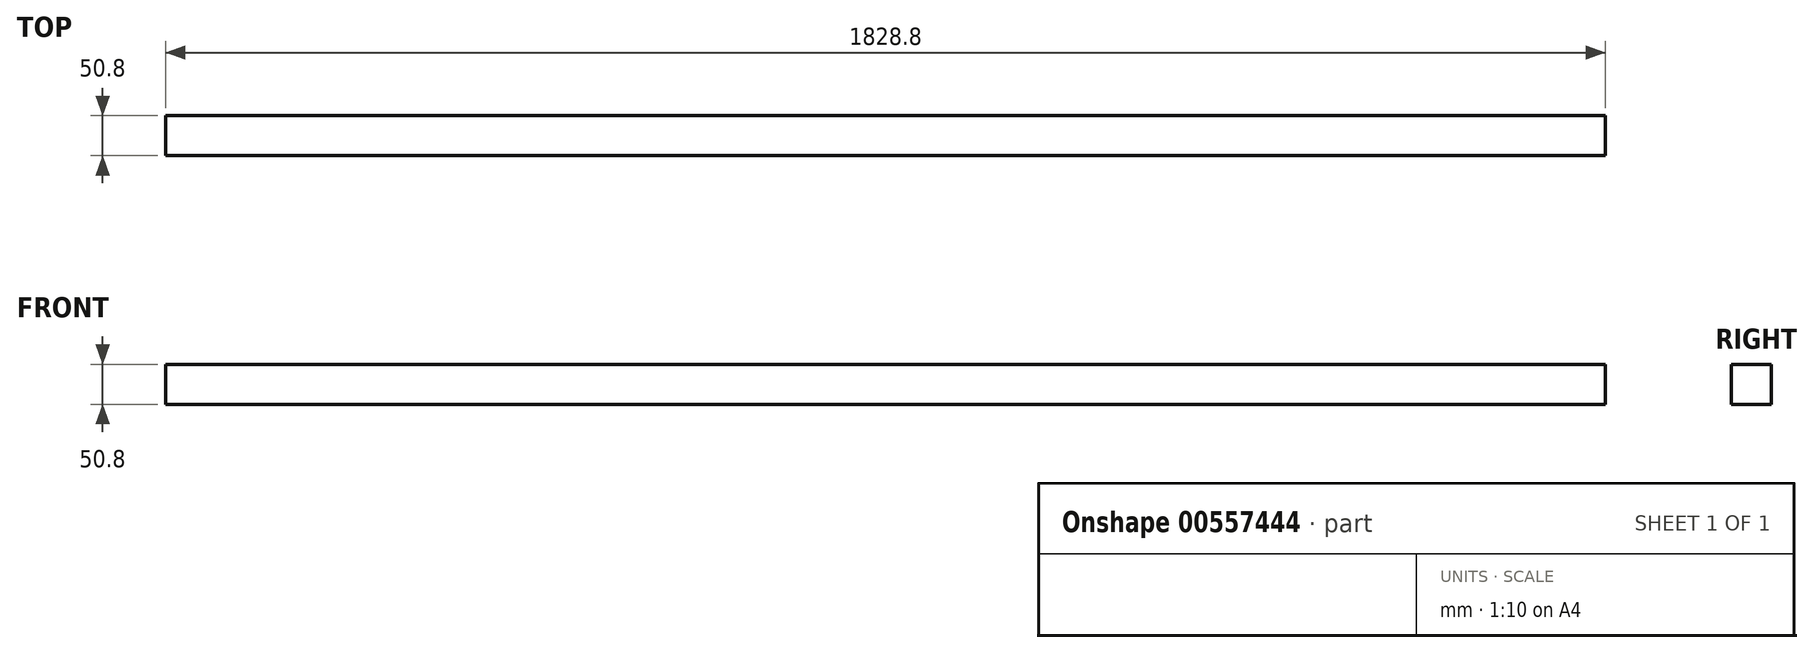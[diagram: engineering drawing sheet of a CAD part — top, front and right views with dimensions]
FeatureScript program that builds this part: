
annotation { "Feature Type Name" : "Feature", "Feature Type Description" : "" }
export const myFeature = defineFeature(function(context is Context, id is Id, definition is map)
    precondition{}
    {
        {
            var Q0;
            Q0=qCreatedBy(makeId("Front.planeOp"),FACE);
            var sketch = newSketch(context, id + "F0", { "sketchPlane" : qUnion([Q0])});
            skLineSegment(sketch, "E0.bottom", {"start": v(0, 50.8) * mm, "end": v(1828.8, 50.8) * mm});
            skLineSegment(sketch, "E0.top", {"start": v(0, 0) * mm, "end": v(1828.8, 0) * mm});
            skLineSegment(sketch, "E0.left", {"start": v(0, 50.8) * mm, "end": v(0, 0) * mm});
            skLineSegment(sketch, "E0.right", {"start": v(1828.8, 50.8) * mm, "end": v(1828.8, 0) * mm});
            skSolve(sketch);
        }
        {
            var Q0;
            Q0=makeQuery(id+"F0.imprint","IMPRINT",FACE,{"disambiguationData":[TD([[makeQuery(id+"F0.imprint","IMPRINT",EDGE,{"derivedFrom":sQuery(id+"F0.wireOp",EDGE,"E0.bottom")}),-1.0]])]});
            extrude(context, id + "F1", {"entities" : qUnion([Q0]), "depth" : 50.8 * mm, "offsetDistance" : 25.4 * mm});
        }
    });
